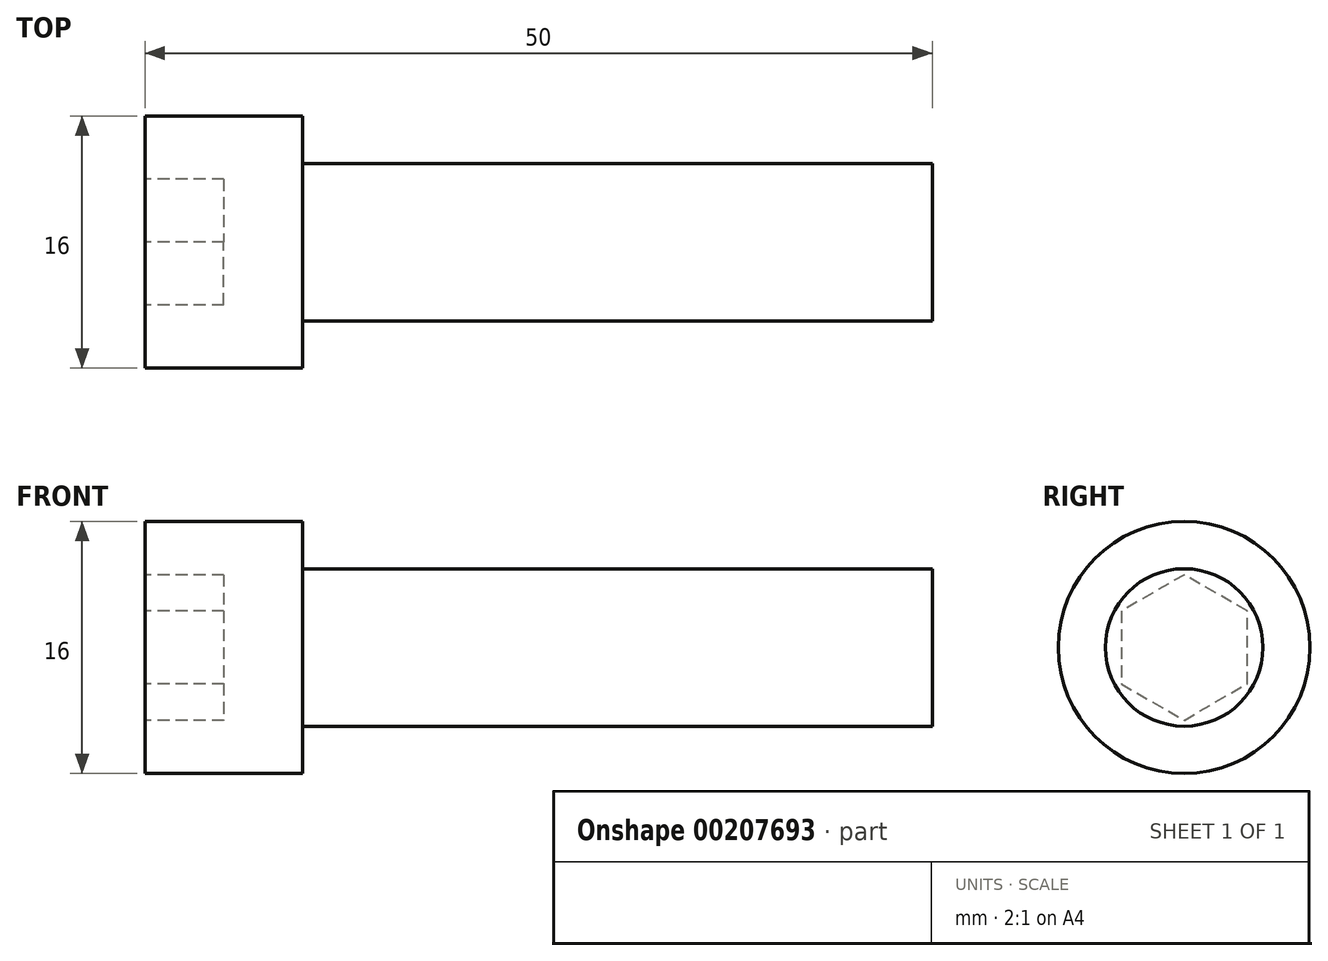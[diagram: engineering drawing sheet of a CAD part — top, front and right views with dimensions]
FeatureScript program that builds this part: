
annotation { "Feature Type Name" : "Feature", "Feature Type Description" : "" }
export const myFeature = defineFeature(function(context is Context, id is Id, definition is map)
    precondition{}
    {
        {
            var Q0;
            Q0=qCreatedBy(makeId("Front.planeOp"),FACE);
            var sketch = newSketch(context, id + "F0", { "sketchPlane" : qUnion([Q0])});
            skLineSegment(sketch, "E0.bottom", {"start": v(0, 5) * mm, "end": v(40, 5) * mm});
            skLineSegment(sketch, "E0.top", {"start": v(0, 0) * mm, "end": v(40, 0) * mm});
            skLineSegment(sketch, "E0.left", {"start": v(0, 5) * mm, "end": v(0, 0) * mm});
            skLineSegment(sketch, "E0.right", {"start": v(40, 5) * mm, "end": v(40, 0) * mm});
            skLineSegment(sketch, "E1.bottom", {"start": v(-10, 8) * mm, "end": v(0, 8) * mm});
            skLineSegment(sketch, "E1.top", {"start": v(-10, 0) * mm, "end": v(0, 0) * mm});
            skLineSegment(sketch, "E1.left", {"start": v(-10, 8) * mm, "end": v(-10, 0) * mm});
            skLineSegment(sketch, "E1.right", {"start": v(0, 8) * mm, "end": v(0, 0) * mm});
            skSolve(sketch);
        }
        {
            var Q0;
            {var subQ2=sQuery(id+"F0.wireOp",EDGE,"E1.bottom");Q0=makeQuery(id+"F0.imprint","IMPRINT",FACE,{"disambiguationData":[TD([[makeQuery(id+"F0.imprint","IMPRINT",EDGE,{"derivedFrom":subQ2}),-1.0]])]});}
            var Q1;
            {var subQ0=sQuery(id+"F0.wireOp",EDGE,"E0.bottom");Q1=makeQuery(id+"F0.imprint","IMPRINT",FACE,{"disambiguationData":[TD([[makeQuery(id+"F0.imprint","IMPRINT",EDGE,{"derivedFrom":subQ0}),-1.0]])]});}
            var Q2;
            Q2=sQuery(id+"F0.wireOp",EDGE,"E0.top");
            revolve(context, id + "F1", {"entities" : qUnion([Q0, Q1]), "axis" : qUnion([Q2]), "revolveType" : RevolveType.FULL});
        }
        {
            var Q0;
            Q0=makeQuery(id+"F1.opRevolve","SWEPT_FACE",FACE,{"disambiguationData":[OSD([sQuery(id+"F0.wireOp",EDGE,"E1.left")])]});
            var sketch = newSketch(context, id + "F2", { "sketchPlane" : qUnion([Q0])});
            skCircle(sketch, "E2.cCircle", {"center": v(0, 0) * mm, "radius": 4 * mm, "construction": true});
            skLineSegment(sketch, "E2.0", {"start": v(4, -2.3) * mm, "end": v(0, -4.62) * mm});
            skLineSegment(sketch, "E2.1", {"start": v(0, -4.62) * mm, "end": v(-4, -2.3) * mm});
            skLineSegment(sketch, "E2.2", {"start": v(-4, -2.3) * mm, "end": v(-4, 2.3) * mm});
            skLineSegment(sketch, "E2.3", {"start": v(-4, 2.3) * mm, "end": v(0, 4.62) * mm});
            skLineSegment(sketch, "E2.4", {"start": v(0, 4.62) * mm, "end": v(4, 2.3) * mm});
            skLineSegment(sketch, "E2.5", {"start": v(4, 2.3) * mm, "end": v(4, -2.3) * mm});
            skPoint(sketch, "E2.0.midPoint", {"position": v(2, -3.46) * mm});
            skSolve(sketch);
        }
        {
            var Q0;
            Q0=makeQuery(id+"F2.imprint","IMPRINT",FACE,{"disambiguationData":[TD([[makeQuery(id+"F2.imprint","IMPRINT",EDGE,{"derivedFrom":sQuery(id+"F2.wireOp",EDGE,"E2.0")}),-1.0]])]});
            extrude(context, id + "F3", {"entities" : qUnion([Q0]), "operationType" : NewBodyOperationType.REMOVE, "oppositeDirection" : true, "depth" : 5 * mm});
        }
    });
